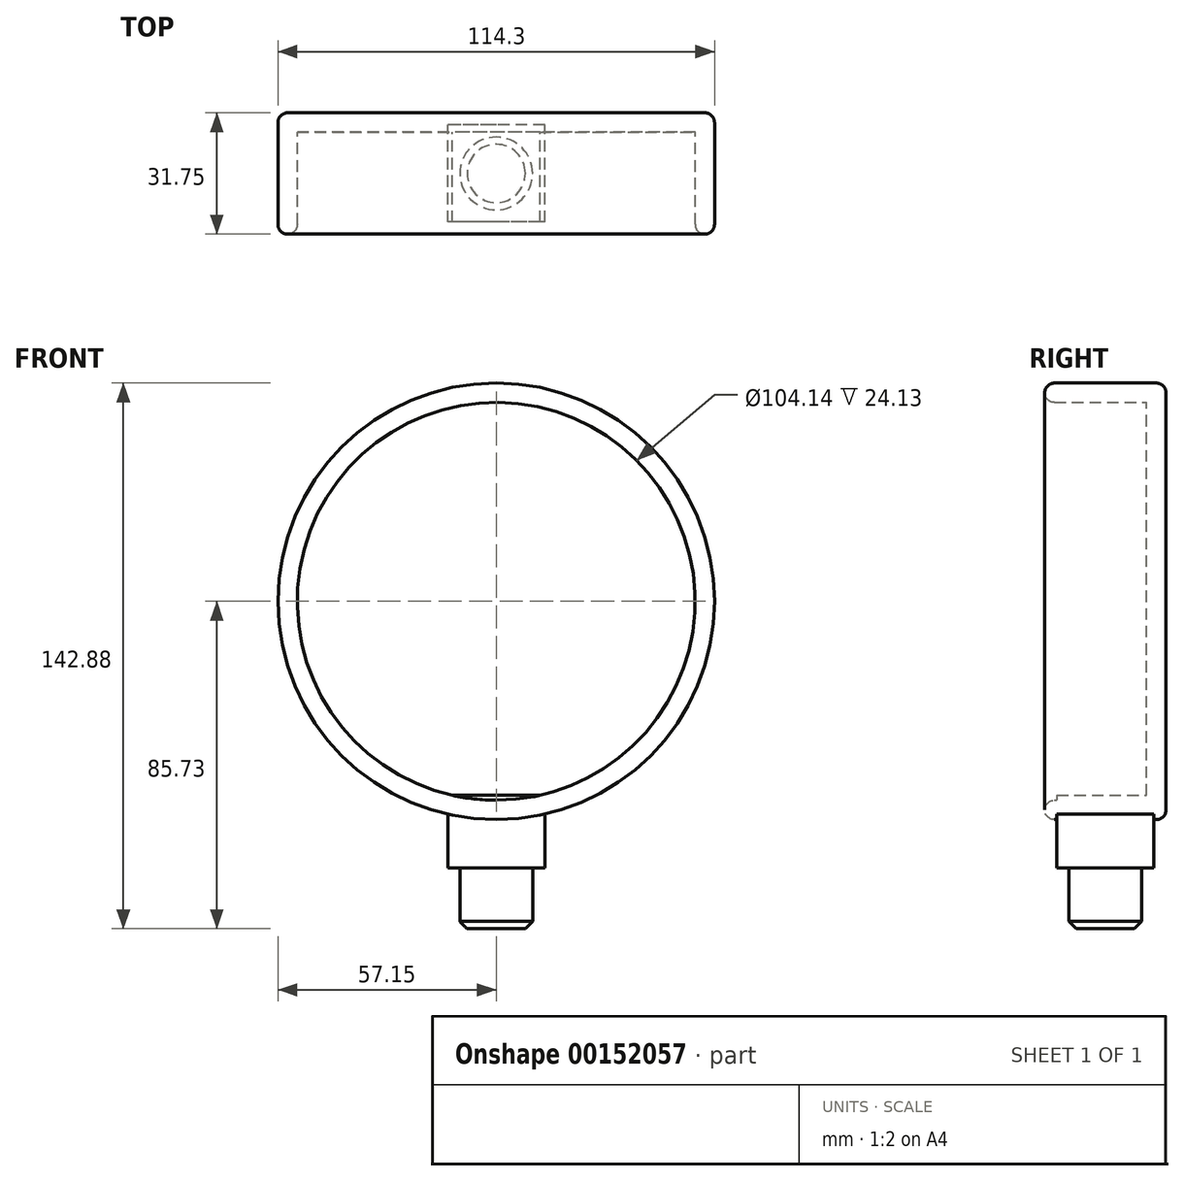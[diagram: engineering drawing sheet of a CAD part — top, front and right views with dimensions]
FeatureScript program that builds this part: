
annotation { "Feature Type Name" : "Feature", "Feature Type Description" : "" }
export const myFeature = defineFeature(function(context is Context, id is Id, definition is map)
    precondition{}
    {
        {
            var Q0;
            Q0=qCreatedBy(makeId("Front.planeOp"),FACE);
            var sketch = newSketch(context, id + "F0", { "sketchPlane" : qUnion([Q0])});
            skCircle(sketch, "E0", {"center": v(0, 0) * mm, "radius": 57.15 * mm});
            skSolve(sketch);
        }
        {
            var Q0;
            Q0 = qSketchRegion(id + "F0", true);
            extrude(context, id + "F1", {"entities" : qUnion([Q0]), "depth" : 31.75 * mm});
        }
        {
            var Q0;
            Q0=makeQuery(id+"F1.opExtrude","CAP_FACE",FACE,{"disambiguationData":[OSD([sQuery(id+"F0.wireOp",EDGE,"E0")])],"isStart":false});
            shell(context, id + "F2", {"entities" : qUnion([Q0]), "thickness" : 5.08 * mm});
        }
        {
            var Q0;
            Q0=qCreatedBy(makeId("Top.planeOp"),FACE);
            cPlane(context, id + "F3", {"entities" : qUnion([Q0]), "cplaneType" : CPlaneType.OFFSET, "offset" : 50.8 * mm, "oppositeDirection" : true, "width" : 152.4 * mm, "height" : 152.4 * mm});
        }
        {
            var Q0;
            Q0=qCreatedBy(id+"F3.planeOp",FACE);
            var sketch = newSketch(context, id + "F4", { "sketchPlane" : qUnion([Q0])});
            skLineSegment(sketch, "E1.bottom", {"start": v(12.7, -28.58) * mm, "end": v(-12.7, -28.58) * mm});
            skLineSegment(sketch, "E1.top", {"start": v(12.7, -3.17) * mm, "end": v(-12.7, -3.17) * mm});
            skLineSegment(sketch, "E1.left", {"start": v(12.7, -28.57) * mm, "end": v(12.7, -3.17) * mm});
            skLineSegment(sketch, "E1.right", {"start": v(-12.7, -28.58) * mm, "end": v(-12.7, -3.17) * mm});
            skPoint(sketch, "E1.middle", {"position": v(0, -15.88) * mm});
            skSolve(sketch);
        }
        {
            var Q0;
            Q0 = qSketchRegion(id + "F4", true);
            extrude(context, id + "F5", {"entities" : qUnion([Q0]), "operationType" : NewBodyOperationType.ADD, "oppositeDirection" : true, "depth" : 19.05 * mm});
        }
        {
            var Q0;
            Q0=makeQuery(id+"F1.opExtrude","CAP_EDGE",EDGE,{"disambiguationData":[OSD([sQuery(id+"F0.wireOp",EDGE,"E0")])],"isStart":false});
            var Q1;
            {var subQ0=sQuery(id+"F0.wireOp",EDGE,"E0");Q1=makeQuery(id+"F2.opShell","OFFSET_EDGE",EDGE,{"disambiguationData":[OSD([subQ0]),TDD([makeQuery(id+"F1.opExtrude","CAP_EDGE",EDGE,{"disambiguationData":[OSD([subQ0])],"isStart":false})])]});}
            var Q2;
            Q2=makeQuery(id+"F1.opExtrude","CAP_EDGE",EDGE,{"disambiguationData":[OSD([sQuery(id+"F0.wireOp",EDGE,"E0")])],"isStart":true});
            fillet(context, id + "F6", {"entities" : qUnion([Q0, Q1, Q2]), "radius" : 2.54 * mm, "tangentPropagation" : true, "allowEdgeOverflow" : false});
        }
        {
            var Q0;
            Q0=makeQuery(id+"F5.opExtrude","CAP_FACE",FACE,{"disambiguationData":[OSD([sQuery(id+"F4.wireOp",EDGE,"E1.bottom"),sQuery(id+"F4.wireOp",EDGE,"E1.top"),sQuery(id+"F4.wireOp",EDGE,"E1.left"),sQuery(id+"F4.wireOp",EDGE,"E1.right")])],"isStart":false});
            var sketch = newSketch(context, id + "F7", { "sketchPlane" : qUnion([Q0])});
            skCircle(sketch, "E2", {"center": v(0, 15.88) * mm, "radius": 9.53 * mm});
            skPoint(sketch, "E2.centerSnap0", {"position": v(-12.7, 15.88) * mm});
            skPoint(sketch, "E2.centerSnap1", {"position": v(0, 3.17) * mm});
            skSolve(sketch);
        }
        {
            var Q0;
            Q0 = qSketchRegion(id + "F7", true);
            extrude(context, id + "F8", {"entities" : qUnion([Q0]), "operationType" : NewBodyOperationType.ADD, "depth" : 15.88 * mm});
        }
        {
            var Q0;
            Q0=makeQuery(id+"F8.opExtrude","CAP_EDGE",EDGE,{"disambiguationData":[OSD([sQuery(id+"F7.wireOp",EDGE,"E2")])],"isStart":false});
            chamfer(context, id + "F9", {"entities" : qUnion([Q0]), "width" : 1.9 * mm, "tangentPropagation" : true});
        }
    });
